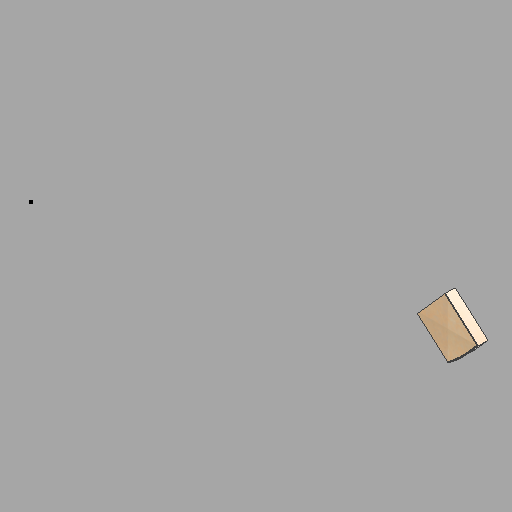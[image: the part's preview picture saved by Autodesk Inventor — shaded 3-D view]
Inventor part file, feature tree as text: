
AUTODESK INVENTOR PART (.ipt)
format: ipt  version: 2022.1 (Build 261234020, 234B)  size: 162,304 bytes
history: native  units: in
note: dims shown in document units (in); Inventor stores cm internally (conversion verified against a paired STEP export)
features: sketch x10, other x3, plane x2
ambient origin geometry x8: Origin, YZ Plane, XZ Plane, XY Plane, X Axis, Y Axis, Z Axis, Center Point
bodies: Solid1 (feature_tree)
feature tree (15):
  other  "Solid18.ipt"
  other  "Solid1::Solid18.ipt"
  other  "TaggingFeature1"
  sketch  "Sketch1"  dims[d0=0.3937in]
  sketch  "Sketch2"
  sketch  "Sketch3"
  sketch  "Sketch4"
  sketch  "Sketch5"
  sketch  "Sketch6"
  sketch  "Sketch8"
  sketch  "Sketch9"
  sketch  "Sketch10"
  sketch  "Sketch11"
  plane  "Work Plane1"
  plane  "Work Plane2"
